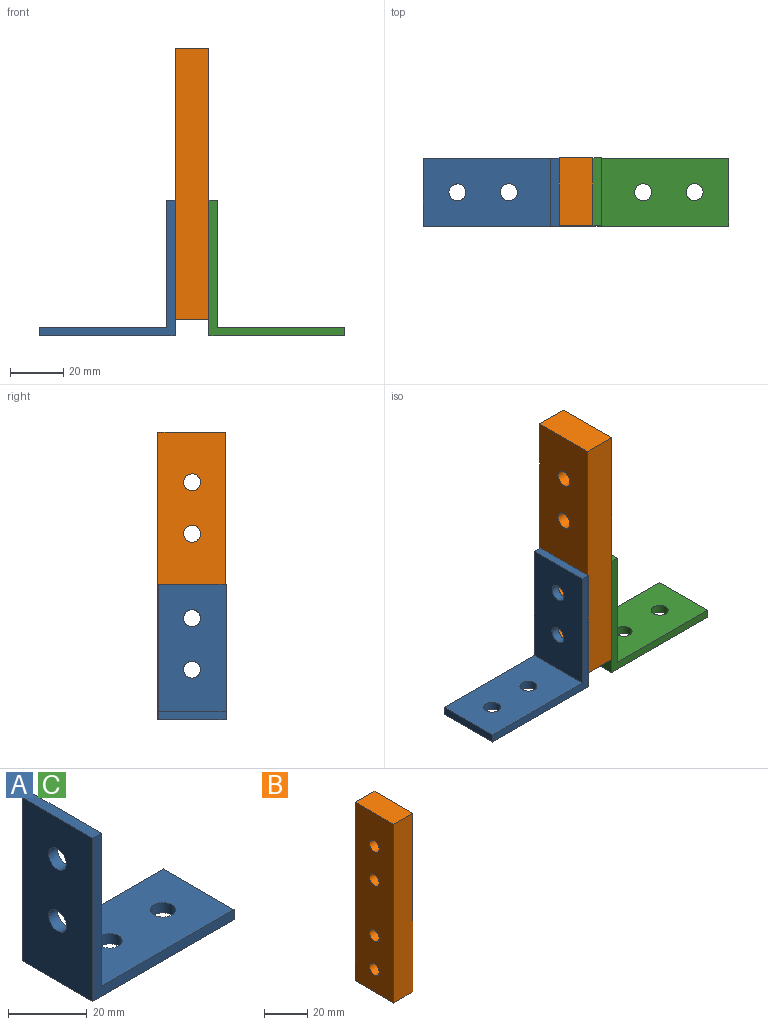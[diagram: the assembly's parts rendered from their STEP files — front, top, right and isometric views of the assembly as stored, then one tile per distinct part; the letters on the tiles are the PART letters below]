
ASSEMBLY  parts=3 mates=2
PART A: 12 faces, bbox 50.8x25.4x50.8 mm
  f0: plane 25.4x3.18mm, normal (0,0,1), area 80.6mm2, adj f1,f5,f6,f7
  f1: plane 50.8x25.4mm, normal (-1,0,0), area 1227mm2, adj f0,f2,f6,f7,f8,f9
  f2: plane 50.8x25.4mm, normal (0,0,-1), area 1227mm2, adj f1,f3,f6,f7,f10,f11
  f3: plane 25.4x3.18mm, normal (1,0,0), area 80.6mm2, adj f2,f4,f6,f7
  f4: plane 47.63x25.4mm, normal (0,0,1), area 1146.3mm2, adj f3,f5,f6,f7,f10,f11
  f5: plane 47.63x25.4mm, normal (1,0,0), area 1146.3mm2, adj f0,f4,f6,f7,f8,f9
  f6: plane 50.8x50.8mm, normal (0,-1,0), area 312.5mm2, adj f0,f1,f2,f3,f4,f5
  f7: plane 50.8x50.8mm, normal (0,1,0), area 312.5mm2, adj f0,f1,f2,f3,f4,f5
  f8: cylinder r=3.17mm len=6.35mm, axis (-1,0,0), area 63.3mm2, adj f1,f5
  f9: cylinder r=3.17mm len=6.35mm, axis (-1,0,0), area 63.3mm2, adj f1,f5
  f10: cylinder r=3.17mm len=6.35mm, axis (0,0,-1), area 63.3mm2, adj f2,f4
  f11: cylinder r=3.17mm len=6.35mm, axis (0,0,-1), area 63.3mm2, adj f2,f4
PART B: 10 faces, bbox 12.7x25.4x101.6 mm
  f0: plane 101.6x12.7mm, normal (0,1,0), area 1290.3mm2, adj f1,f3,f4,f5
  f1: plane 101.6x25.4mm, normal (-1,0,0), area 2454mm2, adj f0,f2,f4,f5,f6,f7,f8,f9
  f2: plane 101.6x12.7mm, normal (0,-1,0), area 1290.3mm2, adj f1,f3,f4,f5
  f3: plane 101.6x25.4mm, normal (1,0,0), area 2454mm2, adj f0,f2,f4,f5,f6,f7,f8,f9
  f4: plane 25.4x12.7mm, normal (0,0,1), area 322.6mm2, adj f0,f1,f2,f3
  f5: plane 25.4x12.7mm, normal (0,0,-1), area 322.6mm2, adj f0,f1,f2,f3
  f6: cylinder r=3.17mm len=12.7mm, axis (-1,0,0), area 253.4mm2, adj f1,f3
  f7: cylinder r=3.17mm len=12.7mm, axis (-1,0,0), area 253.4mm2, adj f1,f3
  f8: cylinder r=3.17mm len=12.7mm, axis (-1,0,0), area 253.4mm2, adj f1,f3
  f9: cylinder r=3.17mm len=12.7mm, axis (-1,0,0), area 253.4mm2, adj f1,f3
PART C: same geometry as A
PLACE A rot(axis=(0,0,-1),180deg) t=(42.04,86.77,34.79)mm
PLACE B rot(axis=(1,0,0),0deg) t=(41.97,74.19,40.78)mm
PLACE C rot(axis=(-1,0,0),0deg) t=(54.74,86.87,34.79)mm
MATE pin_slot B.f9 <-> A.f9  axis (-1,0,0) through (42.04,86.83,53.57)mm
MATE pin_slot C.f8 <-> B.f8  axis (-1,0,0) through (54.74,86.83,72.8)mm
